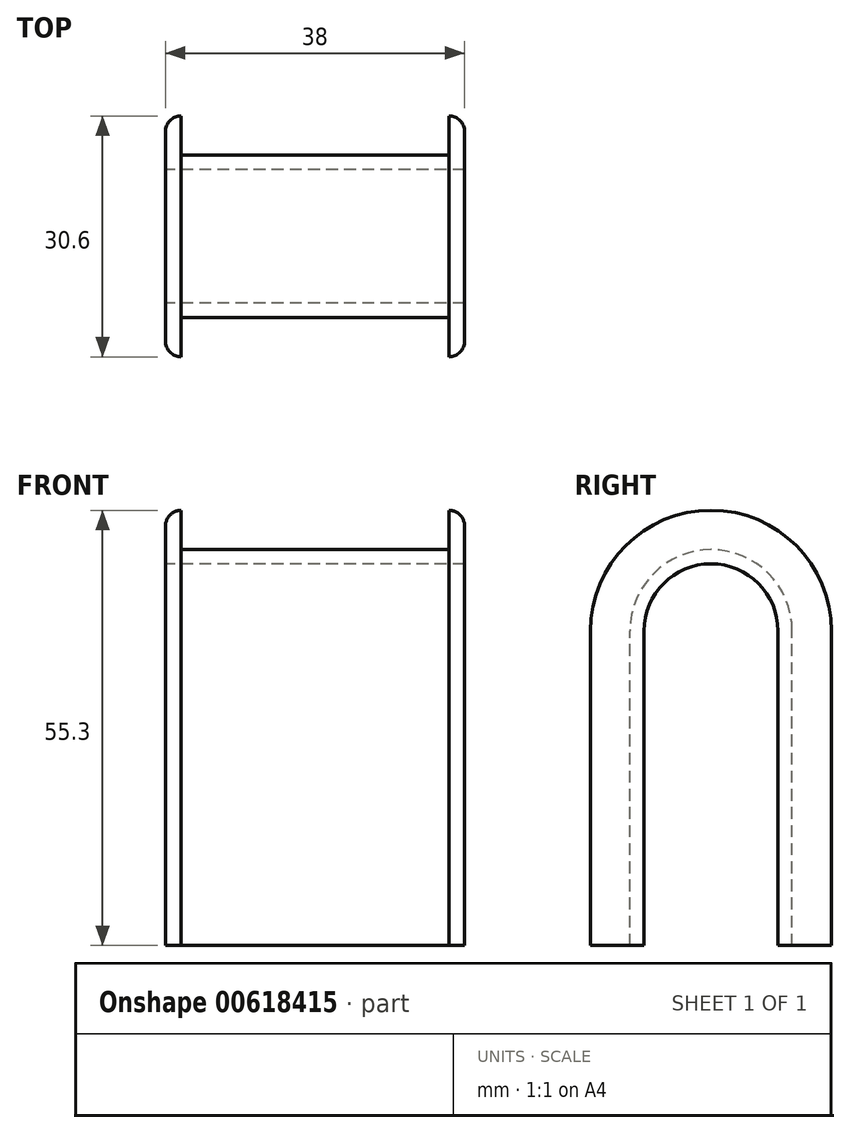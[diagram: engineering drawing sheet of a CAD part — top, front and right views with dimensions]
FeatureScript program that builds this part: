
annotation { "Feature Type Name" : "Feature", "Feature Type Description" : "" }
export const myFeature = defineFeature(function(context is Context, id is Id, definition is map)
    precondition{}
    {
        {
            var Q0;
            Q0=qCreatedBy(makeId("Right.planeOp"),FACE);
            var sketch = newSketch(context, id + "F0", { "sketchPlane" : qUnion([Q0])});
            skLineSegment(sketch, "E0.bottom", {"start": v(0, 0) * mm, "end": v(17, 0) * mm});
            skLineSegment(sketch, "E0.top", {"start": v(0, 40) * mm, "end": v(17, 40) * mm, "construction": true});
            skLineSegment(sketch, "E0.left", {"start": v(0, 0) * mm, "end": v(0, 40) * mm});
            skLineSegment(sketch, "E0.right", {"start": v(17, 0) * mm, "end": v(17, 40) * mm});
            skArc(sketch, "E1", {"start": v(17, 40) * mm, "mid": v(8.5, 48.5) * mm, "end": v(0, 40) * mm});
            skLineSegment(sketch, "E2.0", {"start": v(-1.8, 0) * mm, "end": v(-1.8, 40) * mm});
            skArc(sketch, "E2.1", {"start": v(18.8, 40) * mm, "mid": v(8.5, 50.3) * mm, "end": v(-1.8, 40) * mm});
            skLineSegment(sketch, "E2.2", {"start": v(18.8, 0) * mm, "end": v(18.8, 40) * mm});
            skLineSegment(sketch, "E3", {"start": v(-1.8, 0) * mm, "end": v(0, 0) * mm});
            skLineSegment(sketch, "E4", {"start": v(17, 0) * mm, "end": v(18.8, 0) * mm});
            skLineSegment(sketch, "E5", {"start": v(8.5, 40) * mm, "end": v(8.5, 0) * mm, "construction": true});
            skSolve(sketch);
        }
        {
            var Q0;
            Q0=makeQuery(id+"F0.imprint","IMPRINT",FACE,{"disambiguationData":[TD([[makeQuery(id+"F0.imprint","IMPRINT",EDGE,{"derivedFrom":sQuery(id+"F0.wireOp",EDGE,"E0.left")}),1.0]])]});
            extrude(context, id + "F1", {"entities" : qUnion([Q0]), "depth" : 17 * mm, "offsetDistance" : 25 * mm});
        }
        {
            var Q0;
            Q0=makeQuery(id+"F1.opExtrude","CAP_FACE",FACE,{"disambiguationData":[OSD([sQuery(id+"F0.wireOp",EDGE,"E0.left"),sQuery(id+"F0.wireOp",EDGE,"E0.right"),sQuery(id+"F0.wireOp",EDGE,"E1"),sQuery(id+"F0.wireOp",EDGE,"E2.0"),sQuery(id+"F0.wireOp",EDGE,"E2.1"),sQuery(id+"F0.wireOp",EDGE,"E2.2"),sQuery(id+"F0.wireOp",EDGE,"E3"),sQuery(id+"F0.wireOp",EDGE,"E4")])],"isStart":false});
            var sketch = newSketch(context, id + "F2", { "sketchPlane" : qUnion([Q0])});
            skArc(sketch, "E6.0", {"start": v(18.8, 40) * mm, "mid": v(8.5, 50.3) * mm, "end": v(-1.8, 40) * mm});
            skLineSegment(sketch, "E7.0", {"start": v(-1.8, 0) * mm, "end": v(-1.8, 40) * mm});
            skLineSegment(sketch, "E8.0", {"start": v(18.8, 0) * mm, "end": v(18.8, 40) * mm});
            skArc(sketch, "E9.0", {"start": v(17, 40) * mm, "mid": v(8.5, 48.5) * mm, "end": v(0, 40) * mm});
            skLineSegment(sketch, "E10.0", {"start": v(0, 0) * mm, "end": v(0, 40) * mm});
            skLineSegment(sketch, "E11.0", {"start": v(17, 0) * mm, "end": v(17, 40) * mm});
            skLineSegment(sketch, "E12.0", {"start": v(17, 0) * mm, "end": v(18.8, 0) * mm});
            skLineSegment(sketch, "E13.0", {"start": v(-1.8, 0) * mm, "end": v(0, 0) * mm});
            skLineSegment(sketch, "E14.0", {"start": v(-6.8, 0) * mm, "end": v(-6.8, 40) * mm});
            skArc(sketch, "E14.1", {"start": v(23.8, 40) * mm, "mid": v(8.5, 55.3) * mm, "end": v(-6.8, 40) * mm});
            skLineSegment(sketch, "E14.2", {"start": v(23.8, 0) * mm, "end": v(23.8, 40) * mm});
            skLineSegment(sketch, "E15", {"start": v(-6.8, 0) * mm, "end": v(-1.8, 0) * mm});
            skLineSegment(sketch, "E16", {"start": v(18.8, 0) * mm, "end": v(23.8, 0) * mm});
            skSolve(sketch);
        }
        {
            var Q0;
            Q0=makeQuery(id+"F2.imprint","IMPRINT",FACE,{"disambiguationData":[TD([[makeQuery(id+"F2.imprint","IMPRINT",EDGE,{"derivedFrom":sQuery(id+"F2.wireOp",EDGE,"E6.0")}),-1.0]])]});
            var Q1;
            Q1=makeQuery(id+"F2.imprint","IMPRINT",FACE,{"disambiguationData":[TD([[makeQuery(id+"F2.imprint","IMPRINT",EDGE,{"derivedFrom":sQuery(id+"F2.wireOp",EDGE,"E6.0")}),1.0]])]});
            extrude(context, id + "F3", {"entities" : qUnion([Q0, Q1]), "operationType" : NewBodyOperationType.ADD, "depth" : 2 * mm, "offsetDistance" : 25 * mm});
        }
        {
            var Q0;
            Q0=makeQuery(id+"F3.opExtrude","CAP_EDGE",EDGE,{"disambiguationData":[OSD([sQuery(id+"F2.wireOp",EDGE,"E14.0")])],"isStart":false});
            var Q1;
            Q1=makeQuery(id+"F3.opExtrude","CAP_EDGE",EDGE,{"disambiguationData":[OSD([sQuery(id+"F2.wireOp",EDGE,"E14.1")])],"isStart":false});
            var Q2;
            Q2=makeQuery(id+"F3.opExtrude","CAP_EDGE",EDGE,{"disambiguationData":[OSD([sQuery(id+"F2.wireOp",EDGE,"E14.2")])],"isStart":false});
            fillet(context, id + "F4", {"entities" : qUnion([Q0, Q1, Q2]), "radius" : 2 * mm, "tangentPropagation" : true, "allowEdgeOverflow" : false});
        }
        {
            var Q0;
            Q0=makeQuery(id+"F1.opExtrude","SWEPT_BODY",BODY,{"disambiguationData":[OSD([sQuery(id+"F0.wireOp",EDGE,"E0.left"),sQuery(id+"F0.wireOp",EDGE,"E0.right"),sQuery(id+"F0.wireOp",EDGE,"E1"),sQuery(id+"F0.wireOp",EDGE,"E2.0"),sQuery(id+"F0.wireOp",EDGE,"E2.1"),sQuery(id+"F0.wireOp",EDGE,"E2.2"),sQuery(id+"F0.wireOp",EDGE,"E3"),sQuery(id+"F0.wireOp",EDGE,"E4")])]});
            var Q1;
            Q1=sQuery(id+"F0.wireOp",EDGE,"E5");
            circularPattern(context, id + "F5", {"operationType" : NewBodyOperationType.ADD, "entities" : qUnion([Q0]), "axis" : qUnion([Q1]), "angle" : 360 * degree, "instanceCount" : 2, "equalSpace" : true});
        }
    });
